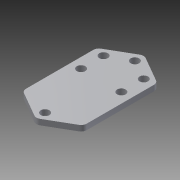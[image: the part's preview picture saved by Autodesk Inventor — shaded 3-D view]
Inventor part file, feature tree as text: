
AUTODESK INVENTOR PART (.ipt)
format: ipt  version: 2014 (Build 180170000, 170)  size: 129,536 bytes
history: native  units: in
note: dims shown in document units (in); Inventor stores cm internally (conversion verified against a paired STEP export)
features: extrude x1, sketch x1
ambient origin geometry x8: Origin, YZ Plane, XZ Plane, XY Plane, X Axis, Y Axis, Z Axis, Center Point
bodies: Solid1 (feature_tree)
feature tree (2):
  extrude  "Extrusion1"  Depth=2.0in
  sketch  "Sketch1"  dims[d1=0.19in d2=2.0in d3=0.19in d4=0.19in d5=0.5in d6=0.4485in d7=0.4485in d8=0.25in d9=0.19in d10=0.19in d11=0.4485in d12=0.5in d14=0.125in d15=0.125in d16=0.0in d17=1.5in d18=1.35in]
